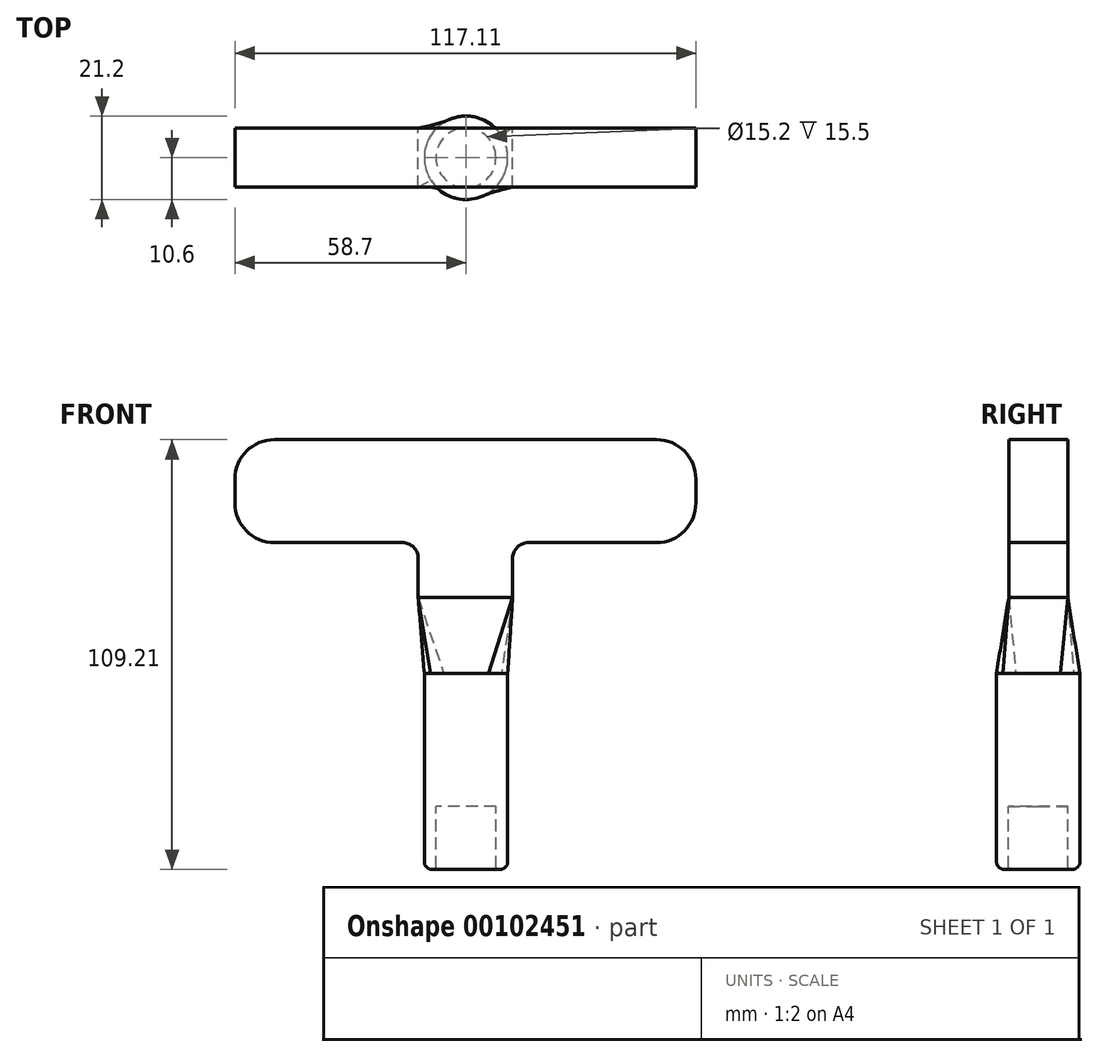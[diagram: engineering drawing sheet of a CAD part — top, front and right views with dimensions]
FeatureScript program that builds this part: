
annotation { "Feature Type Name" : "Feature", "Feature Type Description" : "" }
export const myFeature = defineFeature(function(context is Context, id is Id, definition is map)
    precondition{}
    {
        {
            var Q0;
            Q0=qCreatedBy(makeId("Front.planeOp"),FACE);
            var sketch = newSketch(context, id + "F0", { "sketchPlane" : qUnion([Q0])});
            skLineSegment(sketch, "E0", {"start": v(-7.6, 9.46) * mm, "end": v(-7.6, -6.54) * mm});
            skLineSegment(sketch, "E1", {"start": v(-7.6, -6.54) * mm, "end": v(-10.6, -6.54) * mm});
            skLineSegment(sketch, "E2", {"start": v(0, 43.29) * mm, "end": v(0, 9.46) * mm});
            skLineSegment(sketch, "E3", {"start": v(-7.6, 9.46) * mm, "end": v(0, 9.46) * mm});
            skLineSegment(sketch, "E4", {"start": v(-10.6, 43.29) * mm, "end": v(0, 43.29) * mm});
            skLineSegment(sketch, "E5", {"start": v(-10.6, -6.54) * mm, "end": v(-10.6, 43.29) * mm});
            skSolve(sketch);
        }
        {
            var Q0;
            Q0 = qSketchRegion(id + "F0", true);
            var Q1;
            Q1=sQuery(id+"F0.wireOp",EDGE,"E2");
            revolve(context, id + "F1", {"entities" : qUnion([Q0]), "axis" : qUnion([Q1]), "revolveType" : RevolveType.FULL});
        }
        {
            var Q0;
            Q0=makeQuery(id+"F1.opRevolve","SWEPT_EDGE",EDGE,{"disambiguationData":[OSD([sQuery(id+"F0.wireOp",EDGE,"E0"),sQuery(id+"F0.wireOp",EDGE,"E1")])]});
            fillet(context, id + "F2", {"entities" : qUnion([Q0]), "radius" : .5 * mm, "tangentPropagation" : true, "allowEdgeOverflow" : false});
        }
        {
            var Q0;
            Q0=qCreatedBy(makeId("Front.planeOp"),FACE);
            var sketch = newSketch(context, id + "F3", { "sketchPlane" : qUnion([Q0])});
            skLineSegment(sketch, "E6", {"start": v(-0.14, 62.51) * mm, "end": v(11.86, 62.51) * mm});
            skLineSegment(sketch, "E7", {"start": v(11.86, 62.51) * mm, "end": v(11.86, 72.51) * mm});
            skLineSegment(sketch, "E8", {"start": v(15.86, 76.51) * mm, "end": v(48.4, 76.51) * mm});
            skLineSegment(sketch, "E9", {"start": v(58.4, 86.51) * mm, "end": v(58.4, 92.67) * mm});
            skLineSegment(sketch, "E10", {"start": v(48.4, 102.67) * mm, "end": v(-0.14, 102.67) * mm});
            skPoint(sketch, "E11.visualSharp", {"position": v(58.4, 76.51) * mm});
            skArc(sketch, "E11.filletArc", {"start": v(48.4, 76.51) * mm, "mid": v(55.48, 79.44) * mm, "end": v(58.4, 86.51) * mm});
            skPoint(sketch, "E12.visualSharp", {"position": v(11.86, 76.51) * mm});
            skArc(sketch, "E12.filletArc", {"start": v(15.86, 76.51) * mm, "mid": v(13.03, 75.34) * mm, "end": v(11.86, 72.51) * mm});
            skLineSegment(sketch, "E13", {"start": v(-0.14, 102.67) * mm, "end": v(-0.14, 62.51) * mm});
            skLineSegment(sketch, "E14.MirrorCS", {"start": v(-48.7, 102.67) * mm, "end": v(-0.14, 102.67) * mm});
            skLineSegment(sketch, "E15.MirrorCS", {"start": v(-58.7, 86.51) * mm, "end": v(-58.7, 92.67) * mm});
            skArc(sketch, "E16.MirrorCS", {"start": v(-48.7, 76.51) * mm, "mid": v(-55.77, 79.44) * mm, "end": v(-58.7, 86.51) * mm});
            skLineSegment(sketch, "E17.MirrorCS", {"start": v(-16.14, 76.51) * mm, "end": v(-48.7, 76.51) * mm});
            skArc(sketch, "E18.MirrorCS", {"start": v(-16.14, 76.51) * mm, "mid": v(-13.32, 75.34) * mm, "end": v(-12.14, 72.51) * mm});
            skLineSegment(sketch, "E19.MirrorCS", {"start": v(-12.14, 62.51) * mm, "end": v(-12.14, 72.51) * mm});
            skLineSegment(sketch, "E20.MirrorCS", {"start": v(-0.14, 62.51) * mm, "end": v(-12.14, 62.51) * mm});
            skPoint(sketch, "E21.visualSharp", {"position": v(58.4, 102.67) * mm});
            skArc(sketch, "E21.filletArc", {"start": v(58.4, 92.67) * mm, "mid": v(55.48, 99.74) * mm, "end": v(48.4, 102.67) * mm});
            skPoint(sketch, "E22.visualSharp", {"position": v(-58.7, 102.67) * mm});
            skArc(sketch, "E22.filletArc", {"start": v(-48.7, 102.67) * mm, "mid": v(-55.77, 99.74) * mm, "end": v(-58.7, 92.67) * mm});
            skSolve(sketch);
        }
        {
            var Q0;
            Q0=makeQuery(id+"F3.imprint","IMPRINT",FACE,{"disambiguationData":[TD([[makeQuery(id+"F3.imprint","IMPRINT",EDGE,{"derivedFrom":sQuery(id+"F3.wireOp",EDGE,"E13")}),-1.0]])]});
            var Q1;
            Q1=makeQuery(id+"F3.imprint","IMPRINT",FACE,{"disambiguationData":[TD([[makeQuery(id+"F3.imprint","IMPRINT",EDGE,{"derivedFrom":sQuery(id+"F3.wireOp",EDGE,"E6")}),1.0]])]});
            extrude(context, id + "F4", {"entities" : qUnion([Q0, Q1]), "endBound" : BoundingType.SYMMETRIC, "depth" : 15 * mm});
        }
        {
            var Q1;
            Q1=makeQuery(id+"F4.opExtrude","SWEPT_FACE",FACE,{"disambiguationData":[OSD([sQuery(id+"F3.wireOp",EDGE,"E6"),sQuery(id+"F3.wireOp",EDGE,"E20.MirrorCS")])]});
            var Q2;
            Q2=makeQuery(id+"F1.opRevolve","SWEPT_FACE",FACE,{"disambiguationData":[OSD([sQuery(id+"F0.wireOp",EDGE,"E4")])]});
            loft(context, id + "F5", {"operationType" : NewBodyOperationType.ADD, "sheetProfilesArray" : [{ "sheetProfileEntities" : qUnion([Q1]) }, { "sheetProfileEntities" : qUnion([Q2]) }]});
        }
        {
            var Q0;
            Q0=makeQuery(id+"F1.opRevolve","SWEPT_EDGE",EDGE,{"disambiguationData":[OSD([sQuery(id+"F0.wireOp",EDGE,"E1"),sQuery(id+"F0.wireOp",EDGE,"E5")])]});
            var Q1;
            Q1=makeQuery(id+"F1.opRevolve","SWEPT_FACE",FACE,{"disambiguationData":[OSD([sQuery(id+"F0.wireOp",EDGE,"E1")])]});
            fillet(context, id + "F6", {"entities" : qUnion([Q0, Q1]), "radius" : 2 * mm, "tangentPropagation" : true, "allowEdgeOverflow" : false});
        }
    });
